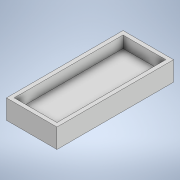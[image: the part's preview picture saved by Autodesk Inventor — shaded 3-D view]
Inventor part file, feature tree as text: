
AUTODESK INVENTOR PART (.ipt)
format: ipt  version: 2021 (Build 250183000, 183)  size: 115,200 bytes
history: native  units: in
note: dims shown in document units (in); Inventor stores cm internally (conversion verified against a paired STEP export)
features: extrude x2, sketch x2, projected_geometry x1
ambient origin geometry x8: Origin, YZ Plane, XZ Plane, XY Plane, X Axis, Y Axis, Z Axis, Center Point
bodies: Solid1 (feature_tree)
feature tree (5):
  extrude  "Extrusion1"  Depth=0.5118in
  extrude  "Extrusion2"  Depth=0.1181in TaperAngle=0.0deg
  sketch  "Sketch1"  dims[d0=1.1811in d1=0.5118in]
  sketch  "Sketch2"  dims[d2=0.0787in d3=0.0in d8=0.1181in d9=0.0in d13=0.0394in d14=0.0394in d15=0.4331in d16=1.1024in]
  projected_geometry  "Projected Loop1"
